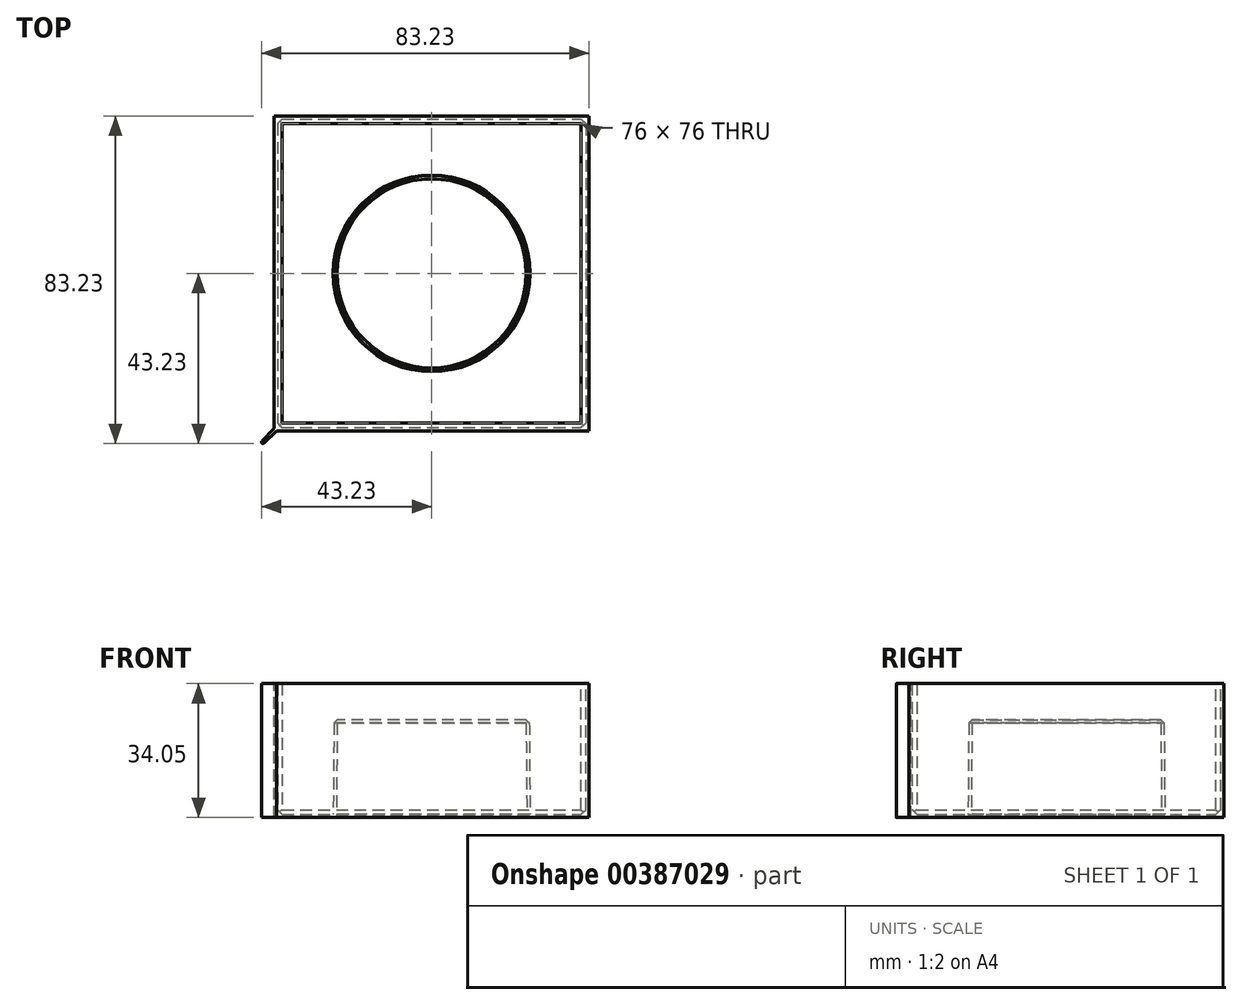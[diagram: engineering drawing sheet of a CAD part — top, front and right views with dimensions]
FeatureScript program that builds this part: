
annotation { "Feature Type Name" : "Feature", "Feature Type Description" : "" }
export const myFeature = defineFeature(function(context is Context, id is Id, definition is map)
    precondition{}
    {
        {
            var Q0;
            Q0=qCreatedBy(makeId("Top.planeOp"),FACE);
            var sketch = newSketch(context, id + "F0", { "sketchPlane" : qUnion([Q0])});
            skLineSegment(sketch, "E0.bottom", {"start": v(-40, 40) * mm, "end": v(40, 40) * mm});
            skLineSegment(sketch, "E0.top", {"start": v(-40, -40) * mm, "end": v(40, -40) * mm});
            skLineSegment(sketch, "E0.left", {"start": v(-40, 40) * mm, "end": v(-40, -40) * mm});
            skLineSegment(sketch, "E0.right", {"start": v(40, 40) * mm, "end": v(40, -40) * mm});
            skPoint(sketch, "E0.middle", {"position": v(0, 0) * mm});
            skSolve(sketch);
        }
        {
            var Q0;
            Q0=qSketchRegion(id+"F0",true);
            extrude(context, id + "F1", {"entities" : qUnion([Q0]), "depth" : 34 * mm});
        }
        {
            var Q0;
            Q0=makeQuery(id+"F1.opExtrude","CAP_FACE",FACE,{"disambiguationData":[OSD([sQuery(id+"F0.wireOp",EDGE,"E0.bottom"),sQuery(id+"F0.wireOp",EDGE,"E0.top"),sQuery(id+"F0.wireOp",EDGE,"E0.left"),sQuery(id+"F0.wireOp",EDGE,"E0.right")])],"isStart":false});
            shell(context, id + "F2", {"entities" : qUnion([Q0]), "thickness" : 0.8 * mm});
        }
        {
            var Q0;
            Q0=makeQuery(id+"F2.opShell","OFFSET_FACE",FACE,{"disambiguationData":[OSD([sQuery(id+"F0.wireOp",EDGE,"E0.bottom"),sQuery(id+"F0.wireOp",EDGE,"E0.top"),sQuery(id+"F0.wireOp",EDGE,"E0.left"),sQuery(id+"F0.wireOp",EDGE,"E0.right")])]});
            var sketch = newSketch(context, id + "F3", { "sketchPlane" : qUnion([Q0])});
            skCircle(sketch, "E1", {"center": v(0, 0) * mm, "radius": 25 * mm});
            skSolve(sketch);
        }
        {
            var Q0;
            Q0=qSketchRegion(id+"F3",true);
            extrude(context, id + "F4", {"entities" : qUnion([Q0]), "operationType" : NewBodyOperationType.ADD, "depth" : 24 * mm, "hasDraft" : true, "draftAngle" : 0.5 * degree, "draftPullDirection" : true});
        }
        {
            var Q0;
            {var subQ0=sQuery(id+"F0.wireOp",EDGE,"E0.left");Q0=makeQuery(id+"F2.opShell","OFFSET_EDGE",EDGE,{"disambiguationData":[OSD([subQ0]),TDD([makeQuery(id+"F1.opExtrude","CAP_EDGE",EDGE,{"disambiguationData":[OSD([subQ0])],"isStart":true})])]});}
            var Q1;
            {var subQ0=sQuery(id+"F0.wireOp",EDGE,"E0.top");Q1=makeQuery(id+"F2.opShell","OFFSET_EDGE",EDGE,{"disambiguationData":[OSD([subQ0]),TDD([makeQuery(id+"F1.opExtrude","CAP_EDGE",EDGE,{"disambiguationData":[OSD([subQ0])],"isStart":true})])]});}
            var Q2;
            {var subQ0=sQuery(id+"F0.wireOp",EDGE,"E0.bottom");Q2=makeQuery(id+"F2.opShell","OFFSET_EDGE",EDGE,{"disambiguationData":[OSD([subQ0]),TDD([makeQuery(id+"F1.opExtrude","CAP_EDGE",EDGE,{"disambiguationData":[OSD([subQ0])],"isStart":true})])]});}
            var Q3;
            {var subQ0=sQuery(id+"F0.wireOp",EDGE,"E0.right");Q3=makeQuery(id+"F2.opShell","OFFSET_EDGE",EDGE,{"disambiguationData":[OSD([subQ0]),TDD([makeQuery(id+"F1.opExtrude","CAP_EDGE",EDGE,{"disambiguationData":[OSD([subQ0])],"isStart":true})])]});}
            var Q4;
            Q4=makeQuery(id+"F4.opExtrude","CAP_EDGE",EDGE,{"disambiguationData":[OSD([sQuery(id+"F3.wireOp",EDGE,"E1")])],"isStart":true});
            chamfer(context, id + "F5", {"entities" : qUnion([Q0, Q1, Q2, Q3, Q4]), "width" : 1.2 * mm, "tangentPropagation" : true});
        }
        {
            var Q0;
            Q0=makeQuery(id+"F1.opExtrude","CAP_FACE",FACE,{"disambiguationData":[OSD([sQuery(id+"F0.wireOp",EDGE,"E0.bottom"),sQuery(id+"F0.wireOp",EDGE,"E0.top"),sQuery(id+"F0.wireOp",EDGE,"E0.left"),sQuery(id+"F0.wireOp",EDGE,"E0.right")])],"isStart":false});
            var sketch = newSketch(context, id + "F6", { "sketchPlane" : qUnion([Q0])});
            skLineSegment(sketch, "E2.0.0", {"start": v(-40, 40) * mm, "end": v(-40, -40) * mm});
            skLineSegment(sketch, "E2.0.1", {"start": v(-40, -40) * mm, "end": v(40, -40) * mm});
            skLineSegment(sketch, "E2.0.2", {"start": v(40, -40) * mm, "end": v(40, 40) * mm});
            skLineSegment(sketch, "E2.0.3", {"start": v(40, 40) * mm, "end": v(-40, 40) * mm});
            skLineSegment(sketch, "E3.bottom", {"start": v(-38, -38) * mm, "end": v(38, -38) * mm});
            skLineSegment(sketch, "E3.top", {"start": v(-38, 38) * mm, "end": v(38, 38) * mm});
            skLineSegment(sketch, "E3.left", {"start": v(-38, -38) * mm, "end": v(-38, 38) * mm});
            skLineSegment(sketch, "E3.right", {"start": v(38, -38) * mm, "end": v(38, 38) * mm});
            skPoint(sketch, "E3.middle", {"position": v(0, 0) * mm});
            skSolve(sketch);
        }
        {
            var Q0;
            Q0=qSketchRegion(id+"F6",true);
            extrude(context, id + "F7", {"entities" : qUnion([Q0]), "operationType" : NewBodyOperationType.ADD, "depth" : 0.05 * mm});
        }
        {
            var Q0;
            {var subQ0=sQuery(id+"F0.wireOp",EDGE,"E0.top");Q0=makeQuery(id+"F2.opShell","OFFSET_EDGE",EDGE,{"disambiguationData":[OSD([subQ0]),TDD([makeQuery(id+"F1.opExtrude","CAP_EDGE",EDGE,{"disambiguationData":[OSD([subQ0])],"isStart":false})])]});}
            var Q1;
            {var subQ0=sQuery(id+"F0.wireOp",EDGE,"E0.left");Q1=makeQuery(id+"F2.opShell","OFFSET_EDGE",EDGE,{"disambiguationData":[OSD([subQ0]),TDD([makeQuery(id+"F1.opExtrude","CAP_EDGE",EDGE,{"disambiguationData":[OSD([subQ0])],"isStart":false})])]});}
            var Q2;
            Q2=makeQuery(id+"F2.opShell","OFFSET_EDGE",EDGE,{"disambiguationData":[OSD([sQuery(id+"F0.wireOp",EDGE,"E0.top"),sQuery(id+"F0.wireOp",EDGE,"E0.left")])]});
            var Q3;
            Q3=makeQuery(id+"F2.opShell","OFFSET_EDGE",EDGE,{"disambiguationData":[OSD([sQuery(id+"F0.wireOp",EDGE,"E0.bottom"),sQuery(id+"F0.wireOp",EDGE,"E0.left")])]});
            var Q4;
            {var subQ0=sQuery(id+"F0.wireOp",EDGE,"E0.bottom");Q4=makeQuery(id+"F2.opShell","OFFSET_EDGE",EDGE,{"disambiguationData":[OSD([subQ0]),TDD([makeQuery(id+"F1.opExtrude","CAP_EDGE",EDGE,{"disambiguationData":[OSD([subQ0])],"isStart":false})])]});}
            var Q5;
            {var subQ0=sQuery(id+"F0.wireOp",EDGE,"E0.right");Q5=makeQuery(id+"F2.opShell","OFFSET_EDGE",EDGE,{"disambiguationData":[OSD([subQ0]),TDD([makeQuery(id+"F1.opExtrude","CAP_EDGE",EDGE,{"disambiguationData":[OSD([subQ0])],"isStart":false})])]});}
            var Q6;
            Q6=makeQuery(id+"F2.opShell","OFFSET_EDGE",EDGE,{"disambiguationData":[OSD([sQuery(id+"F0.wireOp",EDGE,"E0.bottom"),sQuery(id+"F0.wireOp",EDGE,"E0.right")])]});
            var Q7;
            Q7=makeQuery(id+"F2.opShell","OFFSET_EDGE",EDGE,{"disambiguationData":[OSD([sQuery(id+"F0.wireOp",EDGE,"E0.top"),sQuery(id+"F0.wireOp",EDGE,"E0.right")])]});
            chamfer(context, id + "F8", {"entities" : qUnion([Q0, Q1, Q2, Q3, Q4, Q5, Q6, Q7]), "width" : 1.2 * mm, "tangentPropagation" : true});
        }
        {
            var Q0;
            Q0=makeQuery(id+"F4.opExtrude","CAP_EDGE",EDGE,{"disambiguationData":[OSD([sQuery(id+"F3.wireOp",EDGE,"E1")])],"isStart":false});
            chamfer(context, id + "F9", {"entities" : qUnion([Q0]), "width" : 0.8 * mm, "tangentPropagation" : true});
        }
        {
            var Q0;
            Q0=makeQuery(id+"F1.opExtrude","CAP_FACE",FACE,{"disambiguationData":[OSD([sQuery(id+"F0.wireOp",EDGE,"E0.bottom"),sQuery(id+"F0.wireOp",EDGE,"E0.top"),sQuery(id+"F0.wireOp",EDGE,"E0.left"),sQuery(id+"F0.wireOp",EDGE,"E0.right")])],"isStart":true});
            var sketch = newSketch(context, id + "F10", { "sketchPlane" : qUnion([Q0])});
            skLineSegment(sketch, "E4", {"start": v(-40, 40) * mm, "end": v(-42.83, 42.83) * mm});
            skArc(sketch, "E5.0.startCap", {"start": v(-39.72, 40.28) * mm, "mid": v(-39.72, 39.72) * mm, "end": v(-40.28, 39.72) * mm});
            skArc(sketch, "E5.0.endCap", {"start": v(-43.11, 42.55) * mm, "mid": v(-43.11, 43.11) * mm, "end": v(-42.55, 43.11) * mm});
            skLineSegment(sketch, "E5.0.left", {"start": v(-40.28, 39.72) * mm, "end": v(-43.11, 42.55) * mm});
            skLineSegment(sketch, "E5.0.right", {"start": v(-39.72, 40.28) * mm, "end": v(-42.55, 43.11) * mm});
            skLineSegment(sketch, "E6", {"start": v(-40.28, 39.72) * mm, "end": v(-39.73, 39.16) * mm});
            skLineSegment(sketch, "E7", {"start": v(-39.73, 39.16) * mm, "end": v(-39.16, 39.73) * mm});
            skLineSegment(sketch, "E8", {"start": v(-39.72, 40.28) * mm, "end": v(-39.16, 39.73) * mm});
            skSolve(sketch);
        }
        {
            var Q0;
            Q0=qSketchRegion(id+"F10",true);
            var Q1;
            Q1=makeQuery(id+"F7.opExtrude","CAP_FACE",FACE,{"disambiguationData":[OSD([sQuery(id+"F6.wireOp",EDGE,"E2.0.0"),sQuery(id+"F6.wireOp",EDGE,"E2.0.1"),sQuery(id+"F6.wireOp",EDGE,"E2.0.2"),sQuery(id+"F6.wireOp",EDGE,"E2.0.3"),sQuery(id+"F6.wireOp",EDGE,"E3.bottom"),sQuery(id+"F6.wireOp",EDGE,"E3.top"),sQuery(id+"F6.wireOp",EDGE,"E3.left"),sQuery(id+"F6.wireOp",EDGE,"E3.right")])],"isStart":false});
            extrude(context, id + "F11", {"entities" : qUnion([Q0]), "operationType" : NewBodyOperationType.ADD, "endBound" : BoundingType.UP_TO_SURFACE, "oppositeDirection" : true, "endBoundEntityFace" : qUnion([Q1]), "depth" : 25 * mm});
        }
        {
            var Q0;
            Q0=qCreatedBy(makeId("Front.planeOp"),FACE);
            var sketch = newSketch(context, id + "F12", { "sketchPlane" : qUnion([Q0])});
            skLineSegment(sketch, "E9", {"start": v(-25.05, -4.73) * mm, "end": v(-24.79, 25.01) * mm});
            skLineSegment(sketch, "E10.0", {"start": v(-24.23, -2.24) * mm, "end": v(-24, 24) * mm});
            skLineSegment(sketch, "E11.0", {"start": v(24.8, 24) * mm, "end": v(-24.8, 24) * mm});
            skLineSegment(sketch, "E12", {"start": v(-24.23, -2.24) * mm, "end": v(0, -2.24) * mm});
            skLineSegment(sketch, "E13", {"start": v(0, -2.24) * mm, "end": v(0, 24) * mm});
            skSolve(sketch);
        }
        {
            var Q0;
            Q0=qSketchRegion(id+"F12",true);
            var Q1;
            Q1=sQuery(id+"F12.wireOp",EDGE,"E13");
            revolve(context, id + "F13", {"operationType" : NewBodyOperationType.REMOVE, "entities" : qUnion([Q0]), "axis" : qUnion([Q1]), "revolveType" : RevolveType.FULL, "oppositeDirection" : true});
        }
    });
